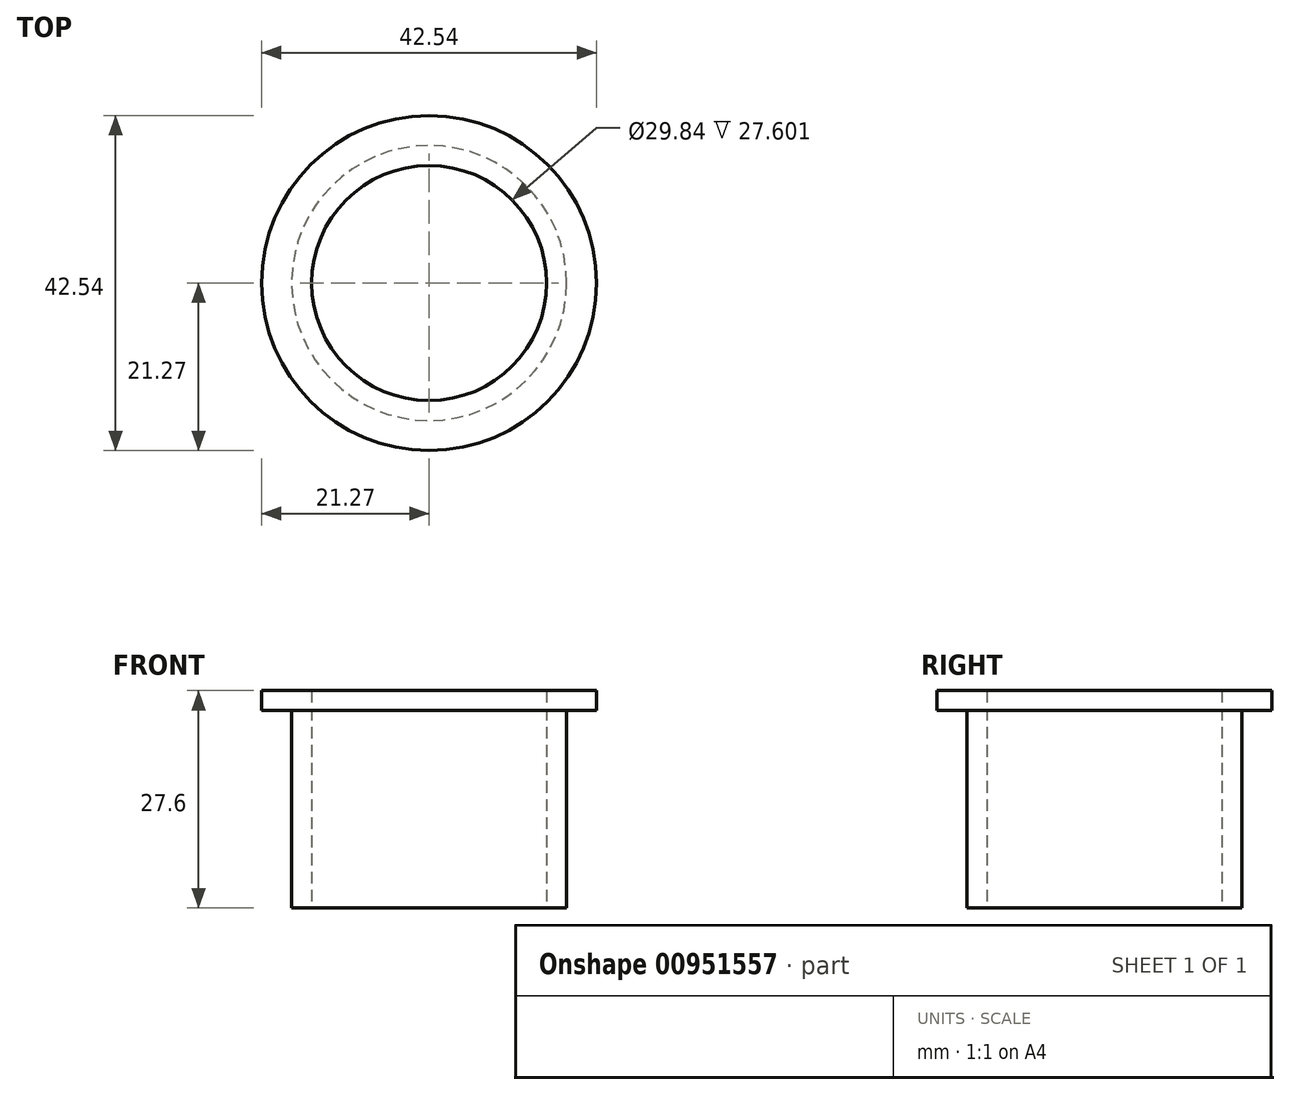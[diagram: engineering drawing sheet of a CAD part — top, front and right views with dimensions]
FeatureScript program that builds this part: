
annotation { "Feature Type Name" : "Feature", "Feature Type Description" : "" }
export const myFeature = defineFeature(function(context is Context, id is Id, definition is map)
    precondition{}
    {
        {
            var Q0;
            Q0=qCreatedBy(makeId("Front.planeOp"),FACE);
            var sketch = newSketch(context, id + "F0", { "sketchPlane" : qUnion([Q0])});
            skLineSegment(sketch, "E0", {"start": v(0, -10.2) * mm, "end": v(0, 20.53) * mm});
            skLineSegment(sketch, "E1", {"start": v(17.46, -10.96) * mm, "end": v(17.46, 14.1) * mm});
            skLineSegment(sketch, "E2", {"start": v(17.46, 14.1) * mm, "end": v(21.27, 14.1) * mm});
            skLineSegment(sketch, "E3", {"start": v(21.27, 14.1) * mm, "end": v(21.27, 16.64) * mm});
            skLineSegment(sketch, "E4", {"start": v(21.27, 16.64) * mm, "end": v(14.92, 16.64) * mm});
            skLineSegment(sketch, "E5", {"start": v(14.92, 16.64) * mm, "end": v(14.92, -10.96) * mm});
            skLineSegment(sketch, "E6", {"start": v(14.92, -10.96) * mm, "end": v(17.46, -10.96) * mm});
            skSolve(sketch);
        }
        {
            var Q0;
            Q0=makeQuery(id+"F0.imprint","IMPRINT",FACE,{"disambiguationData":[TD([[makeQuery(id+"F0.imprint","IMPRINT",EDGE,{"derivedFrom":sQuery(id+"F0.wireOp",EDGE,"E1")}),1.0]])]});
            var Q1;
            Q1=sQuery(id+"F0.wireOp",EDGE,"E0");
            revolve(context, id + "F1", {"surfaceOperationType" : NewSurfaceOperationType.NEW, "entities" : qUnion([Q0]), "axis" : qUnion([Q1]), "revolveType" : RevolveType.FULL});
        }
    });
